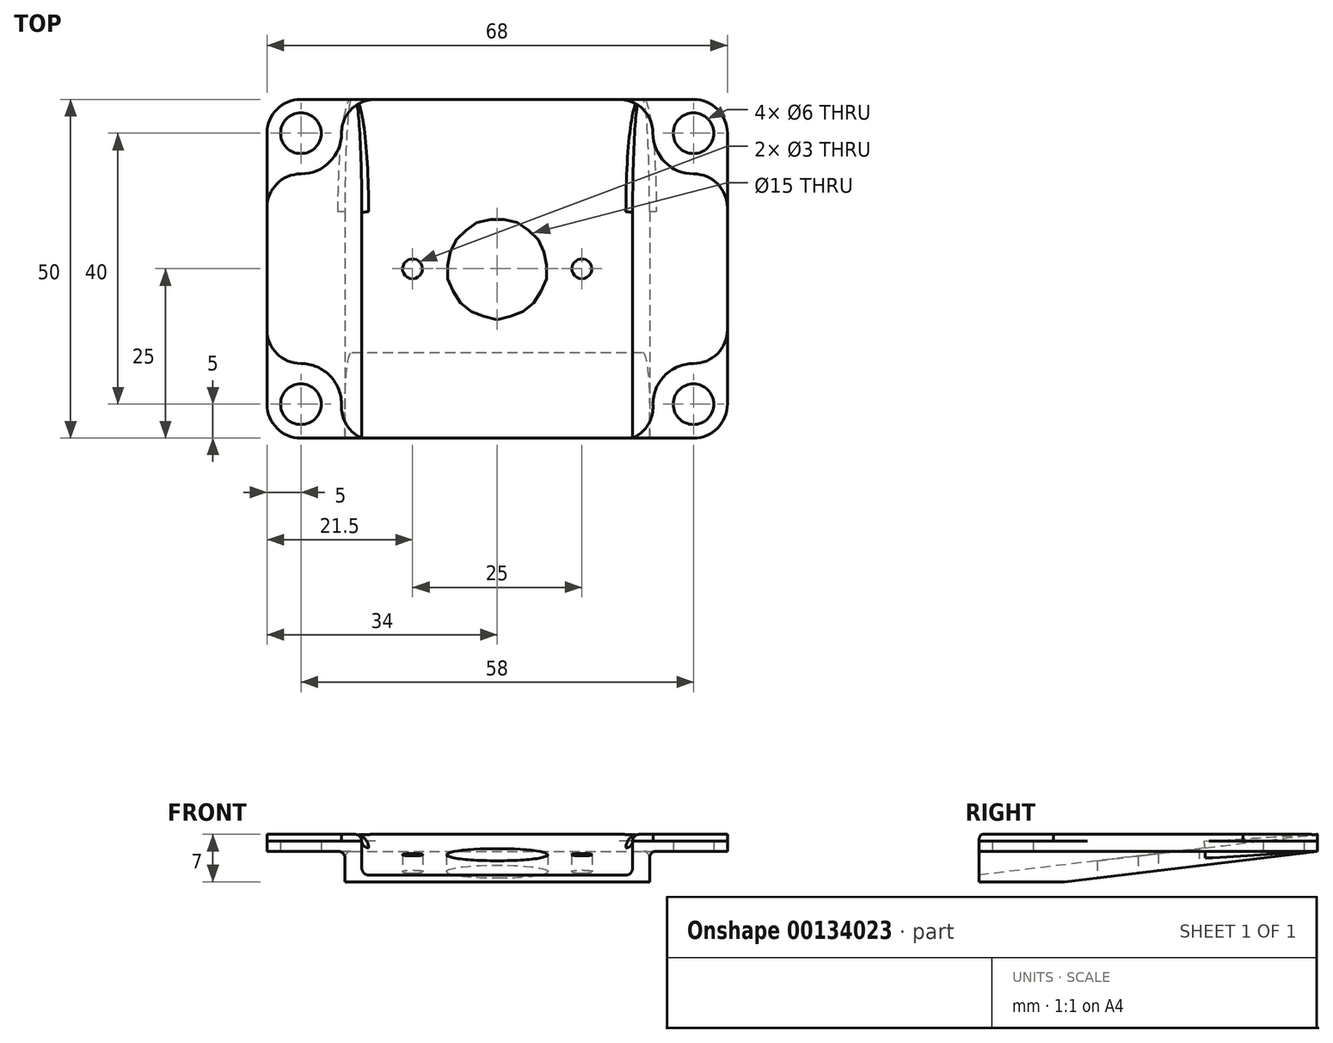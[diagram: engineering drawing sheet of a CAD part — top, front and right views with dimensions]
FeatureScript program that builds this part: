
annotation { "Feature Type Name" : "Feature", "Feature Type Description" : "" }
export const myFeature = defineFeature(function(context is Context, id is Id, definition is map)
    precondition{}
    {
        {
            var Q0;
            Q0=qCreatedBy(makeId("Right.planeOp"),FACE);
            var sketch = newSketch(context, id + "F0", { "sketchPlane" : qUnion([Q0])});
            skLineSegment(sketch, "E0", {"start": v(-25, 0) * mm, "end": v(25, 0) * mm});
            skLineSegment(sketch, "E1", {"start": v(25, 0) * mm, "end": v(25, 8) * mm});
            skLineSegment(sketch, "E2", {"start": v(-25, 8) * mm, "end": v(-25, 0) * mm});
            skLineSegment(sketch, "E3", {"start": v(25, 8) * mm, "end": v(-25, 8) * mm});
            skSolve(sketch);
        }
        {
            var Q0;
            Q0=makeQuery(id+"F0.imprint","IMPRINT",FACE,{"disambiguationData":[TD([[makeQuery(id+"F0.imprint","IMPRINT",EDGE,{"derivedFrom":sQuery(id+"F0.wireOp",EDGE,"E0")}),1.0]])]});
            extrude(context, id + "F1", {"entities" : qUnion([Q0]), "endBound" : BoundingType.SYMMETRIC, "depth" : 68 * mm, "offsetDistance" : 25 * mm});
        }
        {
            var Q0;
            Q0=qCreatedBy(makeId("Right.planeOp"),FACE);
            var sketch = newSketch(context, id + "F2", { "sketchPlane" : qUnion([Q0])});
            skLineSegment(sketch, "E4", {"start": v(25, 8) * mm, "end": v(-25, 2) * mm});
            skLineSegment(sketch, "E5", {"start": v(-25, 2) * mm, "end": v(-25, 14.14) * mm});
            skLineSegment(sketch, "E6", {"start": v(-25, 14.14) * mm, "end": v(25, 14.14) * mm});
            skLineSegment(sketch, "E7", {"start": v(25, 14.14) * mm, "end": v(25, 8) * mm});
            skSolve(sketch);
        }
        {
            var Q0;
            Q0=makeQuery(id+"F2.imprint","IMPRINT",FACE,{"disambiguationData":[TD([[makeQuery(id+"F2.imprint","IMPRINT",EDGE,{"derivedFrom":sQuery(id+"F2.wireOp",EDGE,"E4")}),-1.0]])]});
            extrude(context, id + "F3", {"entities" : qUnion([Q0]), "operationType" : NewBodyOperationType.REMOVE, "endBound" : BoundingType.SYMMETRIC, "oppositeDirection" : true, "depth" : 40 * mm, "offsetDistance" : 25 * mm});
        }
        {
            var Q0;
            Q0=makeQuery(id+"F1.opExtrude","SWEPT_FACE",FACE,{"disambiguationData":[OSD([sQuery(id+"F0.wireOp",EDGE,"E0")])]});
            var Q1;
            Q1=makeQuery(id+"F1.opExtrude","CAP_FACE",FACE,{"disambiguationData":[OSD([sQuery(id+"F0.wireOp",EDGE,"E0"),sQuery(id+"F0.wireOp",EDGE,"E1"),sQuery(id+"F0.wireOp",EDGE,"E2"),sQuery(id+"F0.wireOp",EDGE,"E3")])],"isStart":true});
            var Q2;
            Q2=makeQuery(id+"F1.opExtrude","CAP_FACE",FACE,{"disambiguationData":[OSD([sQuery(id+"F0.wireOp",EDGE,"E0"),sQuery(id+"F0.wireOp",EDGE,"E1"),sQuery(id+"F0.wireOp",EDGE,"E2"),sQuery(id+"F0.wireOp",EDGE,"E3")])],"isStart":false});
            var Q3;
            Q3=makeQuery(id+"F1.opExtrude","SWEPT_FACE",FACE,{"disambiguationData":[OSD([sQuery(id+"F0.wireOp",EDGE,"E2")])]});
            var Q4;
            Q4=makeQuery(id+"F1.opExtrude","SWEPT_FACE",FACE,{"disambiguationData":[OSD([sQuery(id+"F0.wireOp",EDGE,"E1")])]});
            shell(context, id + "F4", {"entities" : qUnion([Q0, Q1, Q2, Q3, Q4]), "thickness" : 2.5 * mm});
        }
        {
            var Q0;
            Q0=qCreatedBy(makeId("Top.planeOp"),FACE);
            var sketch = newSketch(context, id + "F5", { "sketchPlane" : qUnion([Q0])});
            skCircle(sketch, "E8", {"center": v(0, 0) * mm, "radius": 7.5 * mm});
            skCircle(sketch, "E9", {"center": v(-12.5, 0) * mm, "radius": 1.5 * mm});
            skCircle(sketch, "E10", {"center": v(12.5, 0) * mm, "radius": 1.5 * mm});
            skCircle(sketch, "E11", {"center": v(-29, 20) * mm, "radius": 3 * mm});
            skCircle(sketch, "E12", {"center": v(-29, -20) * mm, "radius": 3 * mm});
            skCircle(sketch, "E13", {"center": v(29, -20) * mm, "radius": 3 * mm});
            skCircle(sketch, "E14", {"center": v(29, 20) * mm, "radius": 3 * mm});
            skSolve(sketch);
        }
        {
            var Q0;
            Q0 = qSketchRegion(id + "F5", true);
            extrude(context, id + "F6", {"entities" : qUnion([Q0]), "operationType" : NewBodyOperationType.REMOVE, "depth" : 25 * mm, "offsetDistance" : 25 * mm});
        }
        {
            var Q0;
            Q0=makeQuery(id+"F1.opExtrude","CAP_EDGE",EDGE,{"disambiguationData":[OSD([sQuery(id+"F0.wireOp",EDGE,"E2")])],"isStart":false});
            var Q1;
            Q1=makeQuery(id+"F1.opExtrude","CAP_EDGE",EDGE,{"disambiguationData":[OSD([sQuery(id+"F0.wireOp",EDGE,"E1")])],"isStart":false});
            var Q2;
            Q2=makeQuery(id+"F1.opExtrude","CAP_EDGE",EDGE,{"disambiguationData":[OSD([sQuery(id+"F0.wireOp",EDGE,"E2")])],"isStart":true});
            var Q3;
            Q3=makeQuery(id+"F1.opExtrude","CAP_EDGE",EDGE,{"disambiguationData":[OSD([sQuery(id+"F0.wireOp",EDGE,"E1")])],"isStart":true});
            fillet(context, id + "F7", {"entities" : qUnion([Q0, Q1, Q2, Q3]), "radius" : 5 * mm, "tangentPropagation" : true, "allowEdgeOverflow" : false});
        }
        {
            var Q0;
            Q0=makeQuery(id+"F3.boolean.opBoolean","INTERSECT",EDGE,{"derivedFrom":[makeQuery(id+"F1.opExtrude","SWEPT_FACE",FACE,{"disambiguationData":[OSD([sQuery(id+"F0.wireOp",EDGE,"E3")])]}),makeQuery(id+"F3.opExtrude","CAP_FACE",FACE,{"disambiguationData":[OSD([sQuery(id+"F2.wireOp",EDGE,"E4"),sQuery(id+"F2.wireOp",EDGE,"E5"),sQuery(id+"F2.wireOp",EDGE,"E6"),sQuery(id+"F2.wireOp",EDGE,"E7")])],"isStart":false})]});
            var Q1;
            Q1=makeQuery(id+"F3.boolean.opBoolean","INTERSECT",EDGE,{"derivedFrom":[makeQuery(id+"F1.opExtrude","SWEPT_FACE",FACE,{"disambiguationData":[OSD([sQuery(id+"F0.wireOp",EDGE,"E3")])]}),makeQuery(id+"F3.opExtrude","CAP_FACE",FACE,{"disambiguationData":[OSD([sQuery(id+"F2.wireOp",EDGE,"E4"),sQuery(id+"F2.wireOp",EDGE,"E5"),sQuery(id+"F2.wireOp",EDGE,"E6"),sQuery(id+"F2.wireOp",EDGE,"E7")])],"isStart":true})]});
            var Q2;
            {var subQ0=sQuery(id+"F2.wireOp",EDGE,"E4");Q2=makeQuery(id+"F4.opShell","OFFSET_EDGE",EDGE,{"disambiguationData":[OSD([subQ0]),TDD([makeQuery(id+"F3.boolean.opBoolean","COPY",EDGE,{"derivedFrom":makeQuery(id+"F3.opExtrude","CAP_EDGE",EDGE,{"disambiguationData":[OSD([subQ0])],"isStart":true})})])]});}
            var Q3;
            {var subQ0=sQuery(id+"F2.wireOp",EDGE,"E4");Q3=makeQuery(id+"F4.opShell","OFFSET_EDGE",EDGE,{"disambiguationData":[OSD([subQ0]),TDD([makeQuery(id+"F3.boolean.opBoolean","COPY",EDGE,{"derivedFrom":makeQuery(id+"F3.opExtrude","CAP_EDGE",EDGE,{"disambiguationData":[OSD([subQ0])],"isStart":false})})])]});}
            fillet(context, id + "F8", {"entities" : qUnion([Q0, Q1, Q2, Q3]), "radius" : 1 * mm, "tangentPropagation" : true, "allowEdgeOverflow" : false});
        }
        {
            var Q0;
            Q0=makeQuery(id+"F3.boolean.opBoolean","COPY",EDGE,{"derivedFrom":makeQuery(id+"F3.opExtrude","CAP_EDGE",EDGE,{"disambiguationData":[OSD([sQuery(id+"F2.wireOp",EDGE,"E4")])],"isStart":false})});
            var Q1;
            Q1=makeQuery(id+"F3.boolean.opBoolean","COPY",EDGE,{"derivedFrom":makeQuery(id+"F3.opExtrude","CAP_EDGE",EDGE,{"disambiguationData":[OSD([sQuery(id+"F2.wireOp",EDGE,"E4")])],"isStart":true})});
            var Q2;
            {var subQ0=sQuery(id+"F2.wireOp",EDGE,"E7");var subQ1=sQuery(id+"F2.wireOp",EDGE,"E6");var subQ2=sQuery(id+"F2.wireOp",EDGE,"E5");var subQ3=sQuery(id+"F2.wireOp",EDGE,"E4");var subQ4=sQuery(id+"F0.wireOp",EDGE,"E3");Q2=makeQuery(id+"F4.opShell","OFFSET_EDGE",EDGE,{"disambiguationData":[OSD([subQ4,subQ3,subQ2,subQ1,subQ0]),TDD([makeQuery(id+"F3.boolean.opBoolean","INTERSECT",EDGE,{"derivedFrom":[makeQuery(id+"F1.opExtrude","SWEPT_FACE",FACE,{"disambiguationData":[OSD([subQ4])]}),makeQuery(id+"F3.opExtrude","CAP_FACE",FACE,{"disambiguationData":[OSD([subQ3,subQ2,subQ1,subQ0])],"isStart":false})]})])]});}
            var Q3;
            {var subQ0=sQuery(id+"F2.wireOp",EDGE,"E7");var subQ1=sQuery(id+"F2.wireOp",EDGE,"E6");var subQ2=sQuery(id+"F2.wireOp",EDGE,"E5");var subQ3=sQuery(id+"F2.wireOp",EDGE,"E4");var subQ4=sQuery(id+"F0.wireOp",EDGE,"E3");Q3=makeQuery(id+"F4.opShell","OFFSET_EDGE",EDGE,{"disambiguationData":[OSD([subQ4,subQ3,subQ2,subQ1,subQ0]),TDD([makeQuery(id+"F3.boolean.opBoolean","INTERSECT",EDGE,{"derivedFrom":[makeQuery(id+"F1.opExtrude","SWEPT_FACE",FACE,{"disambiguationData":[OSD([subQ4])]}),makeQuery(id+"F3.opExtrude","CAP_FACE",FACE,{"disambiguationData":[OSD([subQ3,subQ2,subQ1,subQ0])],"isStart":true})]})])]});}
            fillet(context, id + "F9", {"entities" : qUnion([Q0, Q1, Q2, Q3]), "radius" : 1 * mm, "tangentPropagation" : true, "allowEdgeOverflow" : false});
        }
        {
            var Q0;
            Q0=qCreatedBy(makeId("Right.planeOp"),FACE);
            var sketch = newSketch(context, id + "F10", { "sketchPlane" : qUnion([Q0])});
            skLineSegment(sketch, "E15.bottom", {"start": v(-40, 0) * mm, "end": v(40, 0) * mm});
            skLineSegment(sketch, "E15.top", {"start": v(-40, 1) * mm, "end": v(40, 1) * mm});
            skLineSegment(sketch, "E15.left", {"start": v(-40, 0) * mm, "end": v(-40, 1) * mm});
            skLineSegment(sketch, "E15.right", {"start": v(40, 0) * mm, "end": v(40, 1) * mm});
            skSolve(sketch);
        }
        {
            var Q0;
            Q0=makeQuery(id+"F10.imprint","IMPRINT",FACE,{"disambiguationData":[TD([[makeQuery(id+"F10.imprint","IMPRINT",EDGE,{"derivedFrom":sQuery(id+"F10.wireOp",EDGE,"E15.bottom")}),1.0]])]});
            extrude(context, id + "F11", {"entities" : qUnion([Q0]), "operationType" : NewBodyOperationType.REMOVE, "endBound" : BoundingType.SYMMETRIC, "oppositeDirection" : true, "depth" : 200 * mm, "offsetDistance" : 25 * mm});
        }
        {
            var Q0;
            {var subQ0=sQuery(id+"F0.wireOp",EDGE,"E2");var subQ2=sQuery(id+"F0.wireOp",EDGE,"E3");var subQ3=sQuery(id+"F0.wireOp",EDGE,"E1");Q0=makeQuery(id+"F3.boolean.opBoolean","SPLIT",FACE,{"disambiguationData":[TD([makeQuery(id+"F1.opExtrude","CAP_FACE",FACE,{"disambiguationData":[OSD([sQuery(id+"F0.wireOp",EDGE,"E0"),subQ3,subQ0,subQ2])],"isStart":true})])],"derivedFrom":makeQuery(id+"F1.opExtrude","SWEPT_FACE",FACE,{"disambiguationData":[OSD([subQ2])]})});}
            var sketch = newSketch(context, id + "F12", { "sketchPlane" : qUnion([Q0])});
            skCircle(sketch, "E16", {"center": v(-29, -20) * mm, "radius": 6 * mm});
            skCircle(sketch, "E17", {"center": v(29, -20) * mm, "radius": 6 * mm});
            skCircle(sketch, "E18", {"center": v(29, 20) * mm, "radius": 6 * mm});
            skCircle(sketch, "E19", {"center": v(-29, 20) * mm, "radius": 6 * mm});
            skSolve(sketch);
        }
        {
            var Q0;
            Q0 = qSketchRegion(id + "F12", true);
            extrude(context, id + "F13", {"entities" : qUnion([Q0]), "operationType" : NewBodyOperationType.REMOVE, "oppositeDirection" : true, "depth" : 1 * mm, "offsetDistance" : 25 * mm});
        }
        {
            var Q0;
            Q0=makeQuery(id+"F13.boolean.opBoolean","INTERSECT",EDGE,{"derivedFrom":[makeQuery(id+"F1.opExtrude","SWEPT_FACE",FACE,{"disambiguationData":[OSD([sQuery(id+"F0.wireOp",EDGE,"E2")])]}),makeQuery(id+"F13.opExtrude","SWEPT_FACE",FACE,{"disambiguationData":[OSD([sQuery(id+"F12.wireOp",EDGE,"E16")])]})]});
            var Q1;
            Q1=makeQuery(id+"F13.boolean.opBoolean","INTERSECT",EDGE,{"derivedFrom":[makeQuery(id+"F1.opExtrude","CAP_FACE",FACE,{"disambiguationData":[OSD([sQuery(id+"F0.wireOp",EDGE,"E0"),sQuery(id+"F0.wireOp",EDGE,"E1"),sQuery(id+"F0.wireOp",EDGE,"E2"),sQuery(id+"F0.wireOp",EDGE,"E3")])],"isStart":true}),makeQuery(id+"F13.opExtrude","SWEPT_FACE",FACE,{"disambiguationData":[OSD([sQuery(id+"F12.wireOp",EDGE,"E16")])]})]});
            var Q2;
            Q2=makeQuery(id+"F13.boolean.opBoolean","INTERSECT",EDGE,{"derivedFrom":[makeQuery(id+"F1.opExtrude","SWEPT_FACE",FACE,{"disambiguationData":[OSD([sQuery(id+"F0.wireOp",EDGE,"E2")])]}),makeQuery(id+"F13.opExtrude","SWEPT_FACE",FACE,{"disambiguationData":[OSD([sQuery(id+"F12.wireOp",EDGE,"E17")])]})]});
            var Q3;
            Q3=makeQuery(id+"F13.boolean.opBoolean","INTERSECT",EDGE,{"derivedFrom":[makeQuery(id+"F1.opExtrude","CAP_FACE",FACE,{"disambiguationData":[OSD([sQuery(id+"F0.wireOp",EDGE,"E0"),sQuery(id+"F0.wireOp",EDGE,"E1"),sQuery(id+"F0.wireOp",EDGE,"E2"),sQuery(id+"F0.wireOp",EDGE,"E3")])],"isStart":false}),makeQuery(id+"F13.opExtrude","SWEPT_FACE",FACE,{"disambiguationData":[OSD([sQuery(id+"F12.wireOp",EDGE,"E17")])]})]});
            var Q4;
            Q4=makeQuery(id+"F13.boolean.opBoolean","INTERSECT",EDGE,{"derivedFrom":[makeQuery(id+"F1.opExtrude","CAP_FACE",FACE,{"disambiguationData":[OSD([sQuery(id+"F0.wireOp",EDGE,"E0"),sQuery(id+"F0.wireOp",EDGE,"E1"),sQuery(id+"F0.wireOp",EDGE,"E2"),sQuery(id+"F0.wireOp",EDGE,"E3")])],"isStart":false}),makeQuery(id+"F13.opExtrude","SWEPT_FACE",FACE,{"disambiguationData":[OSD([sQuery(id+"F12.wireOp",EDGE,"E18")])]})]});
            var Q5;
            Q5=makeQuery(id+"F13.boolean.opBoolean","INTERSECT",EDGE,{"derivedFrom":[makeQuery(id+"F1.opExtrude","SWEPT_FACE",FACE,{"disambiguationData":[OSD([sQuery(id+"F0.wireOp",EDGE,"E1")])]}),makeQuery(id+"F13.opExtrude","SWEPT_FACE",FACE,{"disambiguationData":[OSD([sQuery(id+"F12.wireOp",EDGE,"E18")])]})]});
            var Q6;
            Q6=makeQuery(id+"F13.boolean.opBoolean","INTERSECT",EDGE,{"derivedFrom":[makeQuery(id+"F1.opExtrude","SWEPT_FACE",FACE,{"disambiguationData":[OSD([sQuery(id+"F0.wireOp",EDGE,"E1")])]}),makeQuery(id+"F13.opExtrude","SWEPT_FACE",FACE,{"disambiguationData":[OSD([sQuery(id+"F12.wireOp",EDGE,"E19")])]})]});
            var Q7;
            Q7=makeQuery(id+"F13.boolean.opBoolean","INTERSECT",EDGE,{"derivedFrom":[makeQuery(id+"F1.opExtrude","CAP_FACE",FACE,{"disambiguationData":[OSD([sQuery(id+"F0.wireOp",EDGE,"E0"),sQuery(id+"F0.wireOp",EDGE,"E1"),sQuery(id+"F0.wireOp",EDGE,"E2"),sQuery(id+"F0.wireOp",EDGE,"E3")])],"isStart":true}),makeQuery(id+"F13.opExtrude","SWEPT_FACE",FACE,{"disambiguationData":[OSD([sQuery(id+"F12.wireOp",EDGE,"E19")])]})]});
            fillet(context, id + "F14", {"entities" : qUnion([Q0, Q1, Q2, Q3, Q4, Q5, Q6, Q7]), "radius" : 5 * mm, "tangentPropagation" : true, "allowEdgeOverflow" : false});
        }
    });
